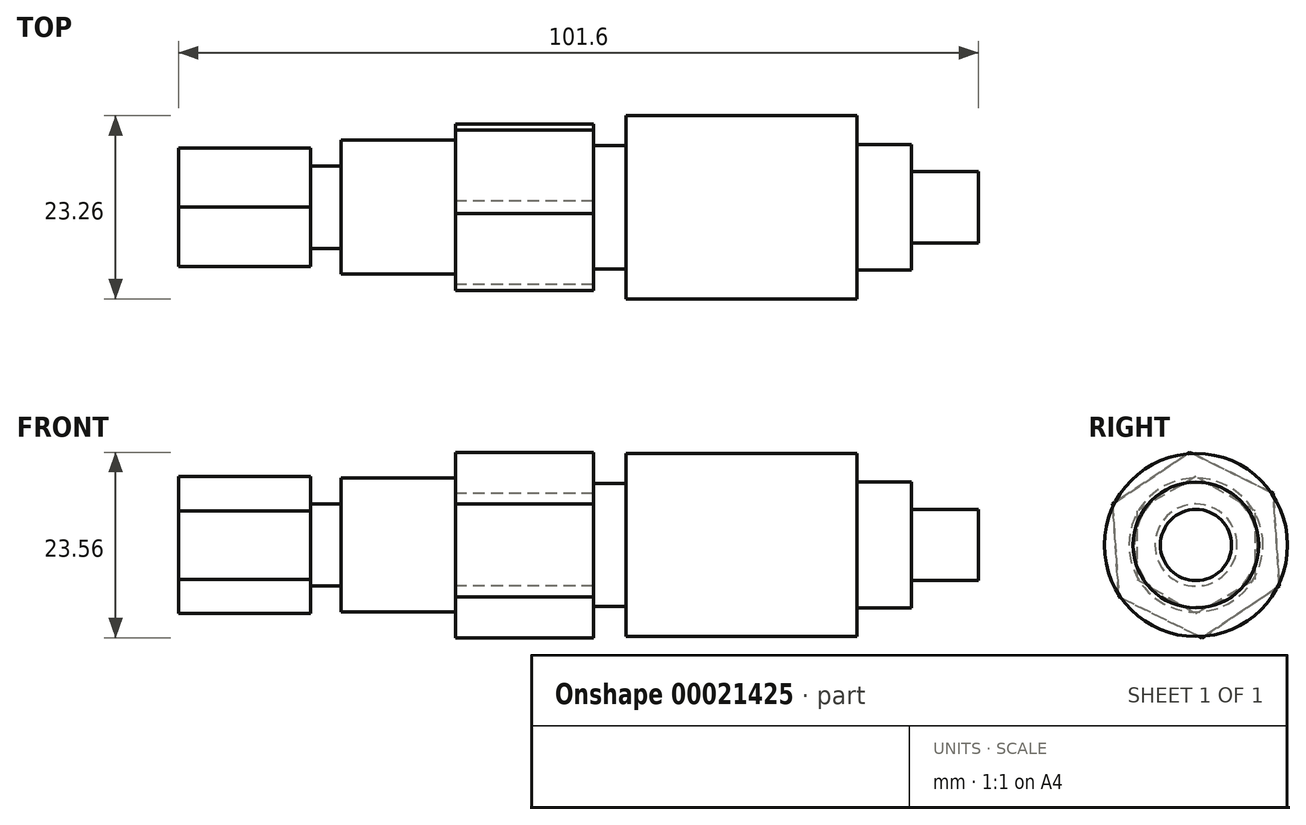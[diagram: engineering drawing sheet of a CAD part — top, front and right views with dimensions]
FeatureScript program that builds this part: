
annotation { "Feature Type Name" : "Feature", "Feature Type Description" : "" }
export const myFeature = defineFeature(function(context is Context, id is Id, definition is map)
    precondition{}
    {
        {
            var Q0;
            Q0=qCreatedBy(makeId("Front.planeOp"),FACE);
            var sketch = newSketch(context, id + "F0", { "sketchPlane" : qUnion([Q0])});
            skLineSegment(sketch, "E0", {"start": v(0, 0) * mm, "end": v(101.6, 0) * mm});
            skLineSegment(sketch, "E1", {"start": v(101.6, 0) * mm, "end": v(101.6, 4.52) * mm});
            skLineSegment(sketch, "E2", {"start": v(101.6, 4.52) * mm, "end": v(93.1, 4.52) * mm});
            skLineSegment(sketch, "E3", {"start": v(93.1, 4.52) * mm, "end": v(93.1, 7.99) * mm});
            skLineSegment(sketch, "E4", {"start": v(93.1, 7.99) * mm, "end": v(86.16, 7.99) * mm});
            skLineSegment(sketch, "E5", {"start": v(86.16, 7.99) * mm, "end": v(86.16, 11.63) * mm});
            skLineSegment(sketch, "E6", {"start": v(86.16, 11.63) * mm, "end": v(56.85, 11.63) * mm});
            skLineSegment(sketch, "E7", {"start": v(56.85, 11.63) * mm, "end": v(56.85, 7.82) * mm});
            skLineSegment(sketch, "E8", {"start": v(56.85, 7.82) * mm, "end": v(52.69, 7.82) * mm});
            skLineSegment(sketch, "E9", {"start": v(52.69, 7.82) * mm, "end": v(52.69, 11.8) * mm});
            skLineSegment(sketch, "E10", {"start": v(52.69, 11.8) * mm, "end": v(35.17, 11.8) * mm});
            skLineSegment(sketch, "E11", {"start": v(35.17, 11.8) * mm, "end": v(35.17, 8.5) * mm});
            skLineSegment(sketch, "E12", {"start": v(35.17, 8.5) * mm, "end": v(20.66, 8.5) * mm});
            skLineSegment(sketch, "E13", {"start": v(20.66, 8.5) * mm, "end": v(20.66, 5.21) * mm});
            skLineSegment(sketch, "E14", {"start": v(20.66, 5.21) * mm, "end": v(16.8, 5.21) * mm});
            skLineSegment(sketch, "E15", {"start": v(16.8, 5.21) * mm, "end": v(16.8, 8.68) * mm});
            skLineSegment(sketch, "E16", {"start": v(16.8, 8.68) * mm, "end": v(0, 8.68) * mm});
            skLineSegment(sketch, "E17", {"start": v(0, 8.68) * mm, "end": v(0, 0) * mm});
            skSolve(sketch);
        }
        {
            var Q0;
            Q0=makeQuery(id+"F0.imprint","IMPRINT",FACE,{"disambiguationData":[TD([[makeQuery(id+"F0.imprint","IMPRINT",EDGE,{"derivedFrom":sQuery(id+"F0.wireOp",EDGE,"E0")}),1.0]])]});
            var Q1;
            Q1=sQuery(id+"F0.wireOp",EDGE,"E0");
            revolve(context, id + "F1", {"entities" : qUnion([Q0]), "axis" : qUnion([Q1]), "revolveType" : RevolveType.FULL});
        }
        {
            var Q0;
            Q0=makeQuery(id+"F1.opRevolve","SWEPT_FACE",FACE,{"disambiguationData":[OSD([sQuery(id+"F0.wireOp",EDGE,"E17")])]});
            var sketch = newSketch(context, id + "F2", { "sketchPlane" : qUnion([Q0])});
            skCircle(sketch, "E18.cCircle", {"center": v(0, 0) * mm, "radius": 8.68 * mm, "construction": true});
            skLineSegment(sketch, "E18.0", {"start": v(7.52, -4.34) * mm, "end": v(0, -8.68) * mm});
            skLineSegment(sketch, "E18.1", {"start": v(0, -8.68) * mm, "end": v(-7.52, -4.34) * mm});
            skLineSegment(sketch, "E18.2", {"start": v(-7.52, -4.34) * mm, "end": v(-7.52, 4.34) * mm});
            skLineSegment(sketch, "E18.3", {"start": v(-7.52, 4.34) * mm, "end": v(0, 8.68) * mm});
            skLineSegment(sketch, "E18.4", {"start": v(0, 8.68) * mm, "end": v(7.52, 4.34) * mm});
            skLineSegment(sketch, "E18.5", {"start": v(7.52, 4.34) * mm, "end": v(7.52, -4.34) * mm});
            skLineSegment(sketch, "E19", {"start": v(0, 0) * mm, "end": v(0, 27.24) * mm, "construction": true});
            skSolve(sketch);
        }
        {
            var Q0;
            {var subQ1=sQuery(id+"F2.wireOp",EDGE,"E18.5");Q0=makeQuery(id+"F2.imprint","IMPRINT",FACE,{"disambiguationData":[TD([[makeQuery(id+"F2.imprint","IMPRINT",EDGE,{"derivedFrom":subQ1}),1.0]])]});}
            var Q1;
            {var subQ1=sQuery(id+"F2.wireOp",EDGE,"E18.1");Q1=makeQuery(id+"F2.imprint","IMPRINT",FACE,{"disambiguationData":[TD([[makeQuery(id+"F2.imprint","IMPRINT",EDGE,{"derivedFrom":subQ1}),1.0]])]});}
            var Q2;
            {var subQ1=sQuery(id+"F2.wireOp",EDGE,"E18.2");Q2=makeQuery(id+"F2.imprint","IMPRINT",FACE,{"disambiguationData":[TD([[makeQuery(id+"F2.imprint","IMPRINT",EDGE,{"derivedFrom":subQ1}),1.0]])]});}
            var Q3;
            {var subQ1=sQuery(id+"F2.wireOp",EDGE,"E18.3");Q3=makeQuery(id+"F2.imprint","IMPRINT",FACE,{"disambiguationData":[TD([[makeQuery(id+"F2.imprint","IMPRINT",EDGE,{"derivedFrom":subQ1}),1.0]])]});}
            var Q4;
            {var subQ1=sQuery(id+"F2.wireOp",EDGE,"E18.0");Q4=makeQuery(id+"F2.imprint","IMPRINT",FACE,{"disambiguationData":[TD([[makeQuery(id+"F2.imprint","IMPRINT",EDGE,{"derivedFrom":subQ1}),1.0]])]});}
            var Q5;
            {var subQ1=sQuery(id+"F2.wireOp",EDGE,"E18.4");Q5=makeQuery(id+"F2.imprint","IMPRINT",FACE,{"disambiguationData":[TD([[makeQuery(id+"F2.imprint","IMPRINT",EDGE,{"derivedFrom":subQ1}),1.0]])]});}
            var Q6;
            Q6=makeQuery(id+"F1.opRevolve","SWEPT_FACE",FACE,{"disambiguationData":[OSD([sQuery(id+"F0.wireOp",EDGE,"E15")])]});
            extrude(context, id + "F3", {"entities" : qUnion([Q0, Q1, Q2, Q3, Q4, Q5]), "operationType" : NewBodyOperationType.REMOVE, "endBound" : BoundingType.UP_TO_SURFACE, "oppositeDirection" : true, "endBoundEntityFace" : qUnion([Q6]), "depth" : 25.4 * mm});
        }
        {
            var Q0;
            Q0=makeQuery(id+"F1.opRevolve","SWEPT_FACE",FACE,{"disambiguationData":[OSD([sQuery(id+"F0.wireOp",EDGE,"E11")])]});
            var sketch = newSketch(context, id + "F4", { "sketchPlane" : qUnion([Q0])});
            skCircle(sketch, "E20.cCircle", {"center": v(0, 0) * mm, "radius": 11.8 * mm, "construction": true});
            skLineSegment(sketch, "E20.0", {"start": v(10.59, 5.22) * mm, "end": v(9.81, -6.56) * mm});
            skLineSegment(sketch, "E20.1", {"start": v(9.81, -6.56) * mm, "end": v(-0.78, -11.78) * mm});
            skLineSegment(sketch, "E20.2", {"start": v(-0.78, -11.78) * mm, "end": v(-10.59, -5.22) * mm});
            skLineSegment(sketch, "E20.3", {"start": v(-10.59, -5.22) * mm, "end": v(-9.81, 6.56) * mm});
            skLineSegment(sketch, "E20.4", {"start": v(-9.81, 6.56) * mm, "end": v(0.78, 11.78) * mm});
            skLineSegment(sketch, "E20.5", {"start": v(0.78, 11.78) * mm, "end": v(10.59, 5.22) * mm});
            skSolve(sketch);
        }
        {
            var Q0;
            {var subQ1=sQuery(id+"F4.wireOp",EDGE,"E20.5");Q0=makeQuery(id+"F4.imprint","IMPRINT",FACE,{"disambiguationData":[TD([[makeQuery(id+"F4.imprint","IMPRINT",EDGE,{"derivedFrom":subQ1}),1.0]])]});}
            var Q1;
            {var subQ1=sQuery(id+"F4.wireOp",EDGE,"E20.0");Q1=makeQuery(id+"F4.imprint","IMPRINT",FACE,{"disambiguationData":[TD([[makeQuery(id+"F4.imprint","IMPRINT",EDGE,{"derivedFrom":subQ1}),1.0]])]});}
            var Q2;
            {var subQ1=sQuery(id+"F4.wireOp",EDGE,"E20.1");Q2=makeQuery(id+"F4.imprint","IMPRINT",FACE,{"disambiguationData":[TD([[makeQuery(id+"F4.imprint","IMPRINT",EDGE,{"derivedFrom":subQ1}),1.0]])]});}
            var Q3;
            {var subQ1=sQuery(id+"F4.wireOp",EDGE,"E20.4");Q3=makeQuery(id+"F4.imprint","IMPRINT",FACE,{"disambiguationData":[TD([[makeQuery(id+"F4.imprint","IMPRINT",EDGE,{"derivedFrom":subQ1}),1.0]])]});}
            var Q4;
            {var subQ1=sQuery(id+"F4.wireOp",EDGE,"E20.3");Q4=makeQuery(id+"F4.imprint","IMPRINT",FACE,{"disambiguationData":[TD([[makeQuery(id+"F4.imprint","IMPRINT",EDGE,{"derivedFrom":subQ1}),1.0]])]});}
            var Q5;
            {var subQ1=sQuery(id+"F4.wireOp",EDGE,"E20.2");Q5=makeQuery(id+"F4.imprint","IMPRINT",FACE,{"disambiguationData":[TD([[makeQuery(id+"F4.imprint","IMPRINT",EDGE,{"derivedFrom":subQ1}),1.0]])]});}
            var Q6;
            Q6=makeQuery(id+"F1.opRevolve","SWEPT_FACE",FACE,{"disambiguationData":[OSD([sQuery(id+"F0.wireOp",EDGE,"E9")])]});
            extrude(context, id + "F5", {"entities" : qUnion([Q0, Q1, Q2, Q3, Q4, Q5]), "operationType" : NewBodyOperationType.REMOVE, "endBound" : BoundingType.UP_TO_SURFACE, "oppositeDirection" : true, "endBoundEntityFace" : qUnion([Q6]), "depth" : 25.4 * mm});
        }
    });
